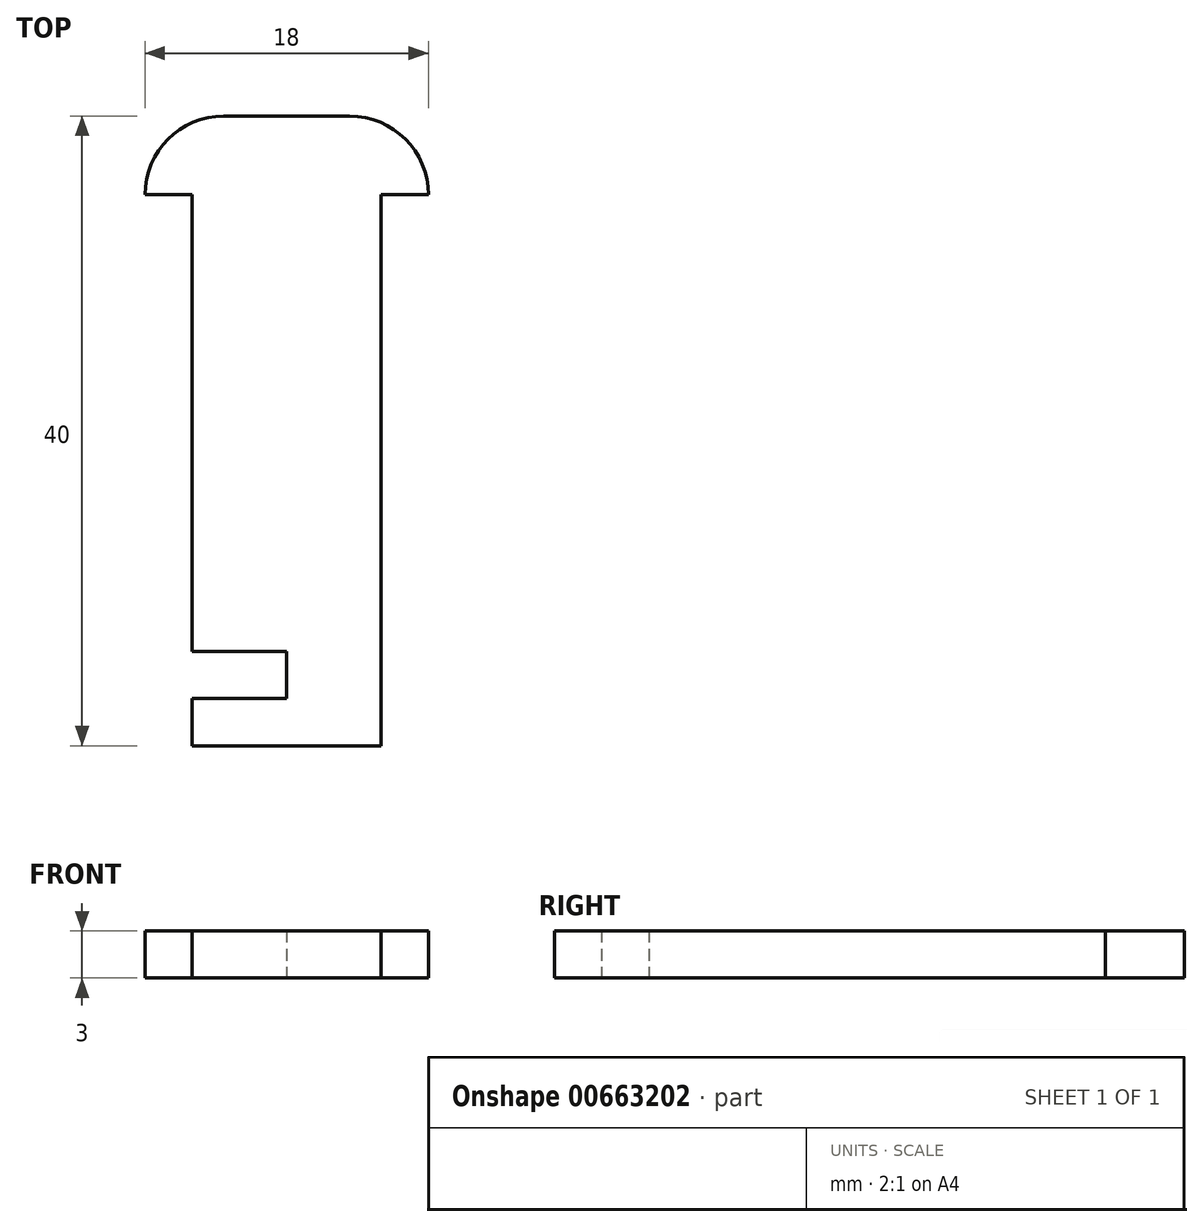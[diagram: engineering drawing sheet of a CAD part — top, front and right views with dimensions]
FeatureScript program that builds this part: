
annotation { "Feature Type Name" : "Feature", "Feature Type Description" : "" }
export const myFeature = defineFeature(function(context is Context, id is Id, definition is map)
    precondition{}
    {
        {
            var Q0;
            Q0=qCreatedBy(makeId("Top.planeOp"),FACE);
            var sketch = newSketch(context, id + "F0", { "sketchPlane" : qUnion([Q0])});
            skLineSegment(sketch, "E0.bottom", {"start": v(-6, 17.5) * mm, "end": v(6, 17.5) * mm});
            skLineSegment(sketch, "E0.top", {"start": v(-6, -17.5) * mm, "end": v(6, -17.5) * mm});
            skLineSegment(sketch, "E0.left", {"start": v(-6, 17.5) * mm, "end": v(-6, -17.5) * mm});
            skLineSegment(sketch, "E0.right", {"start": v(6, 17.5) * mm, "end": v(6, -17.5) * mm});
            skPoint(sketch, "E0.middle", {"position": v(0, 0) * mm});
            skLineSegment(sketch, "E1", {"start": v(-6, 17.5) * mm, "end": v(-9, 17.5) * mm});
            skLineSegment(sketch, "E2", {"start": v(6, 17.5) * mm, "end": v(9, 17.5) * mm});
            skLineSegment(sketch, "E3", {"start": v(-9, 17.5) * mm, "end": v(-9, 17.5) * mm});
            skLineSegment(sketch, "E4", {"start": v(-4, 22.5) * mm, "end": v(4, 22.5) * mm});
            skLineSegment(sketch, "E5", {"start": v(9, 17.5) * mm, "end": v(9, 17.5) * mm});
            skPoint(sketch, "E6.visualSharp", {"position": v(9, 22.5) * mm});
            skArc(sketch, "E6.filletArc", {"start": v(9, 17.5) * mm, "mid": v(7.54, 21.04) * mm, "end": v(4, 22.5) * mm});
            skPoint(sketch, "E7.visualSharp", {"position": v(-9, 22.5) * mm});
            skArc(sketch, "E7.filletArc", {"start": v(-4, 22.5) * mm, "mid": v(-7.54, 21.04) * mm, "end": v(-9, 17.5) * mm});
            skLineSegment(sketch, "E8", {"start": v(-6, -14.5) * mm, "end": v(0, -14.5) * mm});
            skLineSegment(sketch, "E9", {"start": v(0, -14.5) * mm, "end": v(0, -11.5) * mm});
            skLineSegment(sketch, "E10", {"start": v(0, -11.5) * mm, "end": v(-6, -11.5) * mm});
            skSolve(sketch);
        }
        {
            var Q0;
            {var subQ3=sQuery(id+"F0.wireOp",EDGE,"E0.bottom");Q0=makeQuery(id+"F0.imprint","IMPRINT",FACE,{"disambiguationData":[TD([[makeQuery(id+"F0.imprint","IMPRINT",EDGE,{"derivedFrom":subQ3}),-1.0]])]});}
            var Q1;
            Q1=makeQuery(id+"F0.imprint","IMPRINT",FACE,{"disambiguationData":[TD([[makeQuery(id+"F0.imprint","IMPRINT",EDGE,{"derivedFrom":sQuery(id+"F0.wireOp",EDGE,"E0.bottom")}),1.0]])]});
            extrude(context, id + "F1", {"entities" : qUnion([Q0, Q1]), "depth" : 3 * mm, "offsetDistance" : 25 * mm});
        }
    });
